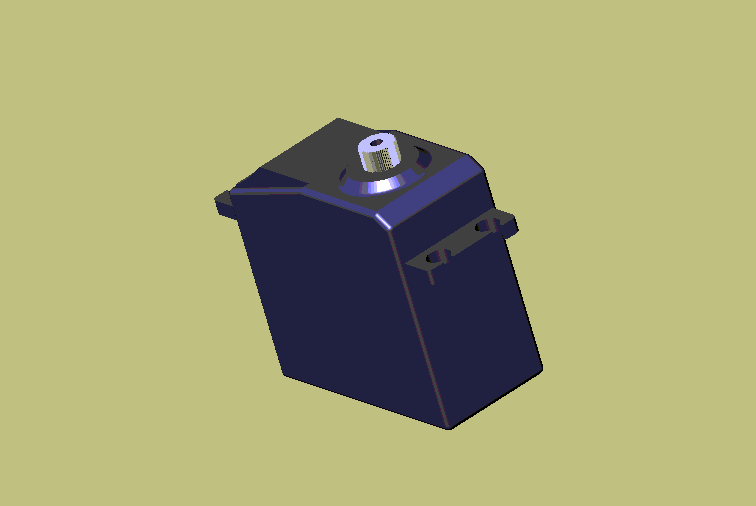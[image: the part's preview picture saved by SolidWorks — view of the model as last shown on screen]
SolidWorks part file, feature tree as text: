
SOLIDWORKS PART (.sldprt)
format: sldprt  version: not decoded by parser v0  size: 357,888 bytes
history: native  units: mm
features: sketch x6, plane x5, extrude x5, fillet x2, material x1, mirror x1, chamfer x1, cut_extrude x1 + 1 further entry (+7 scaffold rows collapsed)
feature tree (30):
  scaffold x7  (default folders/planes/origin — collapsed)
  material  "Matériau <non spécifié>"
  "Corps de surface"
  plane  "Plane1"
  plane  "Plane2"
  plane  "Plane3"
  sketch  "Esquisse1"  dims[c1.D1=6.0mm c1.D3=5.5mm c1.D2=~3.162278mm c2.D2=6.0deg c2.D1=2.75mm c2.D3=3.0mm c2.D4=2.75mm]
  extrude  "Base-Extrusion"  Depth=3.5mm
  sketch  "Esquisse2"  dims[D1=11.5mm]
  extrude  "Boss.-Extru.1"  Depth=1.5mm
  sketch  "Esquisse5"  dims[D1=5.0mm D2=9.0mm D3=9.0mm D4=38.0mm D5=20.0mm D6=5.0mm D7=41.0mm]
  extrude  "Boss.-Extru.2"  Depth=20mm
  fillet  "Congé1"  Radius=1mm
  plane  "Plan1"  Offset=11mm
  sketch  "Esquisse6"  dims[c1.D3=4.0mm c1.D4=2.0mm c1.D1=6.0mm c1.D2=18.0mm c2.D4=2.0mm c2.D5=10.0mm c3.D4=2.5mm]
  extrude  "Boss.-Extru.3"  Depth=2.5mm
  fillet  "Congé3"  Radius=1mm
  plane  "Plan2"  Offset=20.5mm
  mirror  "Symétrie1"
  sketch  "Esquisse7"  dims[D1=16.0mm D2=18.0mm D3=8.0mm]
  extrude  "Boss.-Extru.4"  Depth=5mm
  chamfer  "Chanfrein4"  Distance=3.75mm
  sketch  "Esquisse8"  dims[D1=2.0mm]
  cut_extrude  "Enlèv. mat.-Extru.1"  Depth=10mm
decode coverage: 15 of 16 modeling features carry decoded parameters; 1 rows unclassified (native names shown)
note: ~ marks probable driven/reference dimensions
note: suppression state not decoded; provenance and decode notes live in map.json
